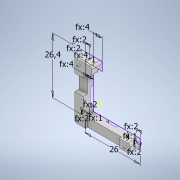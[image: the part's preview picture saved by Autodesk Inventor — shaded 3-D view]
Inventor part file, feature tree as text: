
AUTODESK INVENTOR PART (.ipt)
format: ipt  version: 2022.2 (Build 262287010, 287A)  size: 194,560 bytes
history: native  units: mm
features: extrude x5, sketch x4, chamfer x2, fillet x2
ambient origin geometry x8: Origin, YZ Plane, XZ Plane, XY Plane, X Axis, Y Axis, Z Axis, Center Point
bodies: Volumenkörper1 (feature_tree)
feature tree (13):
  sketch  "Skizze1"  dims[d0=26.0mm d1=26.4mm]
  extrude  "Extrusion1"  Depth=26.4mm
  extrude  "Extrusion2"  Depth=4.0mm
  chamfer  "Fase1"  Distance=1.0mm
  chamfer  "Fase2"  Distance=1.0mm
  extrude  "Extrusion3"  Depth=1.0mm
  extrude  "Extrusion4"  Depth=2.0mm
  fillet  "Rundung1"  Radius=2.0mm
  fillet  "Rundung2"  Radius=2.0mm
  extrude  "Extrusion5"  Depth=2.0mm
  sketch  "Skizze2"  dims[d2=4.0mm d3=4.0mm]
  sketch  "Skizze3"  dims[d4=4.0mm]
  sketch  "Skizze4"  dims[d5=4.0mm d6=1.0mm d7=1.0mm d8=1.0mm d9=2.0mm d10=2.0mm d11=2.0mm d12=2.0mm d13=2.0mm d14=2.0mm d15=4.8mm d16=0.0mm d17=5.7mm d18=0.0mm d19=0.2mm d20=2.0mm d21=45.0deg d22=0.2mm d23=2.0mm d24=45.0deg d25=16.0mm d26=26.0mm d27=5.0mm d28=1.0mm d29=5.7mm d30=0.0mm d31=5.7mm d32=0.0mm d33=2.0mm d34=1.5mm d35=1.0mm d36=1.0mm d37=10.0mm d38=0.0mm]
